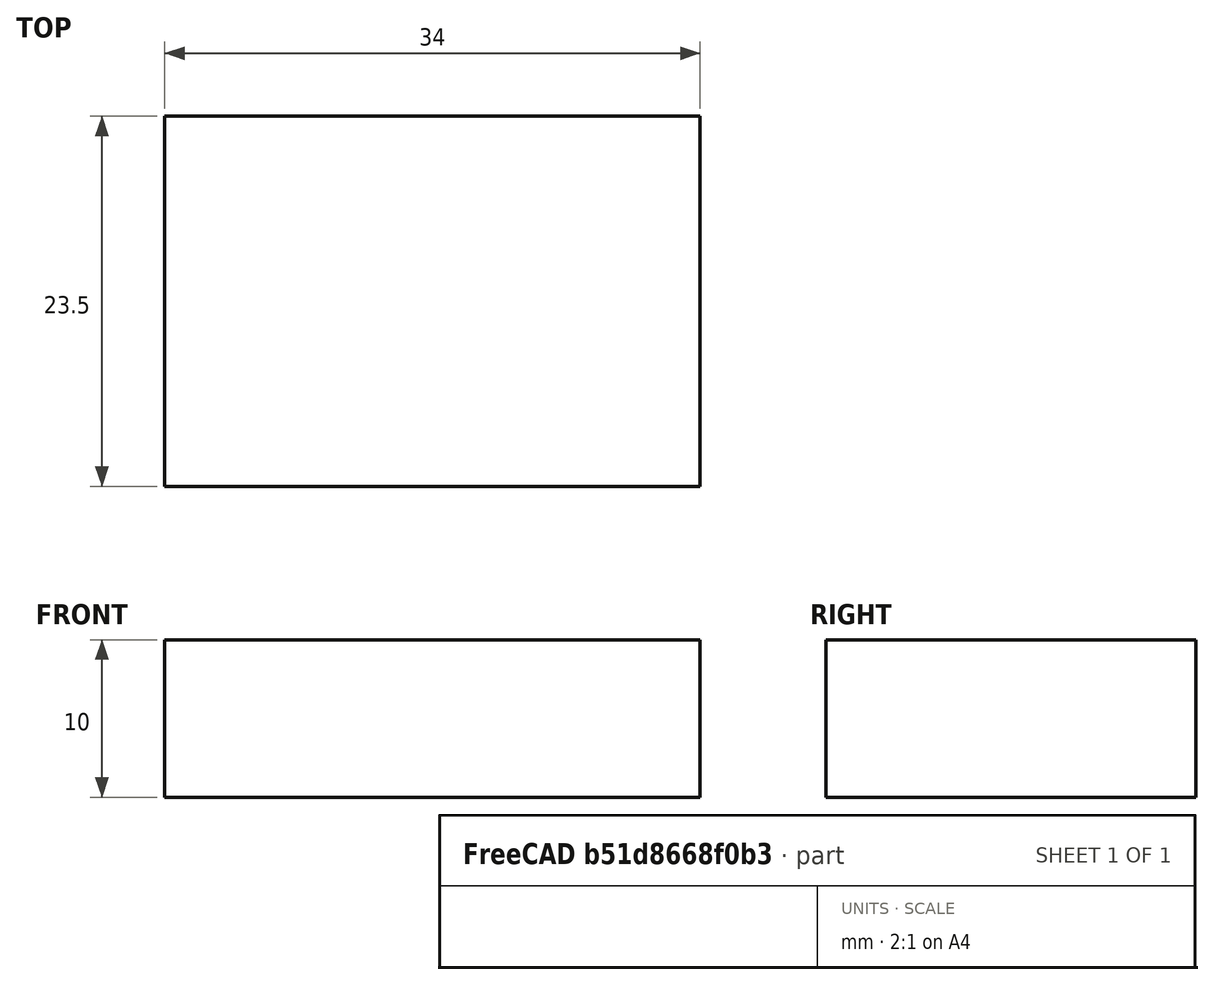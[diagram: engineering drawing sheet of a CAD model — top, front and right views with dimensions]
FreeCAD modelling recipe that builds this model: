
FCSTD DOCUMENT  (FreeCAD 0.18R16131 (Git))
Label: Limit Switch Bed - Top Job
License: All rights reserved
LicenseURL: http://es.wikipedia.org/wiki/Todos_los_derechos_reservados
objects: Path::FeaturePython×16, Part::FeaturePython×2, App::FeaturePython×1, Part::Feature×1, App::DocumentObjectGroup×1, Path::FeatureCompoundPython×1, Mesh::FeaturePython×1
note: 8 computed .brp shape members not serialized (recipe doc carries the construction recipe); baked Part::Feature solids carry a one-line shape summary decoded from their .brp

FEATURE [App::FeaturePython] SetupSheet  # Path/CAM operation (typed FeaturePython)
  ClearanceHeightExpression = OpStockZMax+SetupSheet.ClearanceHeightOffset
  ClearanceHeightOffset = 5
  FinalDepthExpression = OpFinalDepth
  HorizRapid = 0
  SafeHeightExpression = OpStockZMax+SetupSheet.SafeHeightOffset
  SafeHeightOffset = 3
  StartDepthExpression = OpStartDepth
  StepDownExpression = OpToolDiameter
  VertRapid = 0
FEATURE [Path::FeaturePython] T3__SingleFlute2mm  label="T3: SingleFlute2mm"  # Path/CAM operation (typed FeaturePython)
  HorizFeed = 0
  HorizRapid = 0
  SpindleDir = 0
  SpindleSpeed = 0
  ToolNumber = 3
  VertFeed = 0
  VertRapid = 0
  expr: HorizRapid = SetupSheet.HorizRapid
  expr: VertRapid = SetupSheet.VertRapid
FEATURE [Path::FeaturePython] T4__CornTeeth1mm  label="T4: SingleFlute1mm"  # Path/CAM operation (typed FeaturePython)
  HorizFeed = 25
  HorizRapid = 0
  SpindleDir = 0
  SpindleSpeed = 8000
  ToolNumber = 4
  VertFeed = 5
  VertRapid = 0
  expr: HorizRapid = SetupSheet.HorizRapid
  expr: VertRapid = SetupSheet.VertRapid
FEATURE [Path::FeaturePython] T5__Drill1mml  label="T5: Drill1mml"  # Path/CAM operation (typed FeaturePython)
  HorizFeed = 0
  HorizRapid = 0
  SpindleDir = 0
  SpindleSpeed = 0
  ToolNumber = 5
  VertFeed = 0
  VertRapid = 0
  expr: HorizRapid = SetupSheet.HorizRapid
  expr: VertRapid = SetupSheet.VertRapid
FEATURE [Path::FeaturePython] T6__Drill2mm  label="T6: Drill2mm"  # Path/CAM operation (typed FeaturePython)
  HorizFeed = 0
  HorizRapid = 0
  SpindleDir = 0
  SpindleSpeed = 0
  ToolNumber = 6
  VertFeed = 0
  VertRapid = 0
  expr: HorizRapid = SetupSheet.HorizRapid
  expr: VertRapid = SetupSheet.VertRapid
FEATURE [Path::FeaturePython] Contour  label="Interior Contour"  # Path/CAM operation (typed FeaturePython)
  Active = true
  AreaParams:
    Tolerance = 1e-07
    FitArcs = True
    Simplify = False
    CleanDistance = 0.0
    Accuracy = 0.01
    Unit = 1.0
    MinArcPoints = 4
    MaxArcPoints = 100
    ClipperScale = 10000000.0
    Fill = 0
    Coplanar = 2
    Reorient = True
    Outline = False
    Explode = False
    OpenMode = 0
    Deflection = 0.01
    SubjectFill = 0
    ClipFill = 0
    Offset = 0.5
    ExtraPass = 0
    Stepover = 0.0
    LastStepover = 0.0
    JoinType = 0
    EndType = 0
    MiterLimit = 2.0
    RoundPrecision = 0.0
    PocketMode = 0
    ToolRadius = 1.0
    PocketExtraOffset = 0.0
    PocketStepover = 0.0
    PocketLastStepover = 0.0
    FromCenter = False
    Angle = 45.0
    AngleShift = 0.0
    Shift = 0.0
    Thicken = False
    SectionCount = -1
    Stepdown = 1.0
    SectionOffset = 0.0
    SectionTolerance = 1e-06
    SectionMode = 2
    Project = False
  ClearanceHeight = 15
  Direction = 0
  FinalDepth = 3
  JoinType = 0
  MiterLimit = 0.1
  OffsetExtra = 0
  OpFinalDepth = 0
  OpStartDepth = 10
  OpStockZMax = 10
  OpStockZMin = 0
  OpToolDiameter = 1
  PathParams = {'orientation': 1, 'feedrate': 25.0, 'feedrate_v': 5.0, 'verbose': True, 'resume_height': 13.0, 'retraction': 15.0, 'return_end': True, 'preamble': False}
  SafeHeight = 13
  Side = 0
  StartDepth = 10
  StartPoint = (0,0,0)
  StepDown = 1
  ToolController = -> T4__CornTeeth1mm
  UseComp = true
  UseStartPoint = false
  expr: ClearanceHeight = OpStockZMax + SetupSheet.ClearanceHeightOffset
  expr: SafeHeight = OpStockZMax + SetupSheet.SafeHeightOffset
  expr: StepDown = OpToolDiameter
  expr: FinalDepth = 3
  expr: StartDepth = OpStartDepth
FEATURE [Path::FeaturePython] Contour001  label="Exterior Contour"  # Path/CAM operation (typed FeaturePython)
  Active = true
  AreaParams:
    Tolerance = 1e-07
    FitArcs = True
    Simplify = False
    CleanDistance = 0.0
    Accuracy = 0.01
    Unit = 1.0
    MinArcPoints = 4
    MaxArcPoints = 100
    ClipperScale = 10000000.0
    Fill = 0
    Coplanar = 2
    Reorient = True
    Outline = False
    Explode = False
    OpenMode = 0
    Deflection = 0.01
    SubjectFill = 0
    ClipFill = 0
    Offset = 0.7
    ExtraPass = 0
    Stepover = 0.0
    LastStepover = 0.0
    JoinType = 0
    EndType = 0
    MiterLimit = 2.0
    RoundPrecision = 0.0
    PocketMode = 0
    ToolRadius = 1.0
    PocketExtraOffset = 0.0
    PocketStepover = 0.0
    PocketLastStepover = 0.0
    FromCenter = False
    Angle = 45.0
    AngleShift = 0.0
    Shift = 0.0
    Thicken = False
    SectionCount = -1
    Stepdown = 1.0
    SectionOffset = 0.0
    SectionTolerance = 1e-06
    SectionMode = 2
    Project = False
  ClearanceHeight = 15
  Direction = 0
  FinalDepth = 3
  JoinType = 0
  MiterLimit = 0.1
  OffsetExtra = 0.2
  OpFinalDepth = 0
  OpStartDepth = 10
  OpStockZMax = 10
  OpStockZMin = 0
  OpToolDiameter = 1
  PathParams = {'orientation': 1, 'feedrate': 25.0, 'feedrate_v': 5.0, 'verbose': True, 'resume_height': 13.0, 'retraction': 15.0, 'return_end': True, 'preamble': False}
  SafeHeight = 13
  Side = 0
  StartDepth = 10
  StartPoint = (0,0,0)
  StepDown = 3
  ToolController = -> T4__CornTeeth1mm
  UseComp = true
  UseStartPoint = false
  expr: ClearanceHeight = OpStockZMax + SetupSheet.ClearanceHeightOffset
  expr: SafeHeight = OpStockZMax + SetupSheet.SafeHeightOffset
  expr: StepDown = 3
  expr: FinalDepth = 3
  expr: StartDepth = OpStartDepth
FEATURE [Path::FeaturePython] Contour002  # Path/CAM operation (typed FeaturePython)
  Active = true
  AreaParams:
    Tolerance = 1e-07
    FitArcs = True
    Simplify = False
    CleanDistance = 0.0
    Accuracy = 0.01
    Unit = 1.0
    MinArcPoints = 4
    MaxArcPoints = 100
    ClipperScale = 10000000.0
    Fill = 0
    Coplanar = 2
    Reorient = True
    Outline = False
    Explode = False
    OpenMode = 0
    Deflection = 0.01
    SubjectFill = 0
    ClipFill = 0
    Offset = 0.6
    ExtraPass = 0
    Stepover = 0.0
    LastStepover = 0.0
    JoinType = 0
    EndType = 0
    MiterLimit = 2.0
    RoundPrecision = 0.0
    PocketMode = 0
    ToolRadius = 1.0
    PocketExtraOffset = 0.0
    PocketStepover = 0.0
    PocketLastStepover = 0.0
    FromCenter = False
    Angle = 45.0
    AngleShift = 0.0
    Shift = 0.0
    Thicken = False
    SectionCount = -1
    Stepdown = 1.0
    SectionOffset = 0.0
    SectionTolerance = 1e-06
    SectionMode = 2
    Project = False
  ClearanceHeight = 15
  Direction = 0
  FinalDepth = 0
  JoinType = 0
  MiterLimit = 0.1
  OffsetExtra = 0.1
  OpFinalDepth = 0
  OpStartDepth = 10
  OpStockZMax = 10
  OpStockZMin = 0
  OpToolDiameter = 1
  PathParams = {'orientation': 1, 'feedrate': 25.0, 'feedrate_v': 5.0, 'verbose': True, 'resume_height': 13.0, 'retraction': 15.0, 'return_end': True, 'preamble': False}
  SafeHeight = 13
  Side = 0
  StartDepth = 3
  StartPoint = (0,0,0)
  StepDown = 1
  ToolController = -> T4__CornTeeth1mm
  UseComp = true
  UseStartPoint = false
  expr: ClearanceHeight = OpStockZMax + SetupSheet.ClearanceHeightOffset
  expr: SafeHeight = OpStockZMax + SetupSheet.SafeHeightOffset
  expr: StepDown = OpToolDiameter
  expr: FinalDepth = OpFinalDepth
  expr: StartDepth = 3
FEATURE [Path::FeaturePython] TagDressup  label="Bottom Contourn"  # Path/CAM operation (typed FeaturePython)
  Angle = 60
  Base = -> Contour002
  Height = 0.5
  Positions = (5) [(24,-0.6,0),(8,-0.6,0),(-0.6,10.75,0),(8.5,22.1,0),(32.6,10,0)]
  Radius = 0
  SegmentationFactor = 50
  Width = 1.5
FEATURE [Part::Feature] Part__Feature  label="LimitSwitchBed"
  shape: bbox 32 x 21.5 x 10 mm, 57 faces (baked)
FEATURE [Part::FeaturePython] Clone  label="Model-Body"  # Draft clone (typed FeaturePython)
  AttacherType = Attacher::AttachEngine3D
  Fuse = false
  Objects = -> [Part__Feature]
  PathResource = Model
  Scale = (1,1,1)
FEATURE [App::DocumentObjectGroup] Model
  Group = -> [Clone]
FEATURE [Part::FeaturePython] Stock  # WARN: FeaturePython — macro-defined, semantics opaque (R4)
  Base = -> Model
  ExtXneg = 1
  ExtXpos = 1
  ExtYneg = 1
  ExtYpos = 1
  ExtZneg = 0
  ExtZpos = 0
  StockType = FromBase
FEATURE [Path::FeaturePython] Pocket_Shape001  # Path/CAM operation (typed FeaturePython)
  Active = true
  AreaParams:
    Tolerance = 1e-07
    FitArcs = True
    Simplify = False
    CleanDistance = 0.0
    Accuracy = 0.01
    Unit = 1.0
    MinArcPoints = 4
    MaxArcPoints = 100
    ClipperScale = 10000000.0
    Fill = 0
    Coplanar = 0
    Reorient = True
    Outline = False
    Explode = False
    OpenMode = 0
    Deflection = 0.01
    SubjectFill = 0
    ClipFill = 0
    Offset = 0.0
    ExtraPass = 0
    Stepover = 0.0
    LastStepover = 0.0
    JoinType = 0
    EndType = 0
    MiterLimit = 2.0
    RoundPrecision = 0.0
    PocketMode = 3
    ToolRadius = 0.5
    PocketExtraOffset = 0.0
    PocketStepover = 1.0
    PocketLastStepover = 0.0
    FromCenter = True
    Angle = 45.0
    AngleShift = 0.0
    Shift = 0.0
    Thicken = False
    SectionCount = -1
    Stepdown = 1.0
    SectionOffset = 0.0
    SectionTolerance = 1e-06
    SectionMode = 2
    Project = False
  Base = -> [Clone]
  ClearanceHeight = 15
  CutMode = 0
  ExtraOffset = 0
  FinalDepth = 6
  FinishDepth = 0
  KeepToolDown = false
  MinTravel = false
  OffsetPattern = 2
  OpFinalDepth = 6
  OpStartDepth = 10
  OpStockZMax = 10
  OpStockZMin = 0
  OpToolDiameter = 1
  PathParams = {'orientation': 1, 'feedrate': 25.0, 'feedrate_v': 5.0, 'verbose': True, 'resume_height': 13.0, 'retraction': 15.0, 'return_end': True, 'preamble': False}
  SafeHeight = 13
  StartAt = 0
  StartDepth = 10
  StartPoint = (0,0,0)
  StepDown = 0.5
  StepOver = 100
  ToolController = -> T4__CornTeeth1mm
  UseOutline = false
  UseStartPoint = false
  ZigZagAngle = 45
  expr: ClearanceHeight = OpStockZMax + SetupSheet.ClearanceHeightOffset
  expr: SafeHeight = OpStockZMax + SetupSheet.SafeHeightOffset
  expr: StepDown = OpToolDiameter / 2
  expr: FinalDepth = OpFinalDepth
  expr: StartDepth = OpStartDepth
FEATURE [Path::FeaturePython] Pocket_Shape  # Path/CAM operation (typed FeaturePython)
  Active = true
  AreaParams:
    Tolerance = 1e-07
    FitArcs = True
    Simplify = False
    CleanDistance = 0.0
    Accuracy = 0.01
    Unit = 1.0
    MinArcPoints = 4
    MaxArcPoints = 100
    ClipperScale = 10000000.0
    Fill = 0
    Coplanar = 0
    Reorient = True
    Outline = False
    Explode = False
    OpenMode = 0
    Deflection = 0.01
    SubjectFill = 0
    ClipFill = 0
    Offset = 0.0
    ExtraPass = 0
    Stepover = 0.0
    LastStepover = 0.0
    JoinType = 0
    EndType = 0
    MiterLimit = 2.0
    RoundPrecision = 0.0
    PocketMode = 2
    ToolRadius = 0.5
    PocketExtraOffset = 0.0
    PocketStepover = 0.5
    PocketLastStepover = 0.0
    FromCenter = True
    Angle = 45.0
    AngleShift = 0.0
    Shift = 0.0
    Thicken = False
    SectionCount = -1
    Stepdown = 1.0
    SectionOffset = 0.0
    SectionTolerance = 1e-06
    SectionMode = 2
    Project = False
  Base = -> [Clone]
  ClearanceHeight = 15
  CutMode = 0
  ExtraOffset = 0
  FinalDepth = 4
  FinishDepth = 0
  KeepToolDown = false
  MinTravel = false
  OffsetPattern = 1
  OpFinalDepth = 4
  OpStartDepth = 10
  OpStockZMax = 10
  OpStockZMin = 0
  OpToolDiameter = 1
  PathParams = {'orientation': 1, 'feedrate': 25.0, 'feedrate_v': 5.0, 'verbose': True, 'resume_height': 13.0, 'retraction': 15.0, 'return_end': True, 'preamble': False}
  SafeHeight = 13
  StartAt = 0
  StartDepth = 10
  StartPoint = (0,0,0)
  StepDown = 1
  StepOver = 50
  ToolController = -> T4__CornTeeth1mm
  UseOutline = false
  UseStartPoint = false
  ZigZagAngle = 45
  expr: ClearanceHeight = OpStockZMax + SetupSheet.ClearanceHeightOffset
  expr: SafeHeight = OpStockZMax + SetupSheet.SafeHeightOffset
  expr: StepDown = OpToolDiameter
  expr: FinalDepth = OpFinalDepth
  expr: StartDepth = OpStartDepth
FEATURE [Path::FeaturePython] DogboneDressup001  label="SwitchBed"  # Path/CAM operation (typed FeaturePython)
  Base = -> Pocket_Shape
  BoneBlacklist = [5,6,7,8,9,10,11,12,13,14,15,16,17,18,19,20,25,26,27,28,29,30,31,32,33,34,39,40,41,42,43,44,45,46,47,48,53,54,55,56,57,58,59,60,61,62,67,68,69,70,71,72,73,74,75,76,81,82,83]
  Custom = 0
  Incision = 0
  Side = 1
  Style = 0
FEATURE [Path::FeaturePython] DogboneDressup  # Path/CAM operation (typed FeaturePython)
  Base = -> Pocket_Shape001
  BoneBlacklist = [1,10,11,20,21,30,31,40,41,50,51,60,61,70,71,80]
  Custom = 0.6
  Incision = 2
  Side = 0
  Style = 2
FEATURE [Path::FeaturePython] DogboneDressup002  # Path/CAM operation (typed FeaturePython)
  Base = -> DogboneDressup
  BoneBlacklist = [2,3,4,5,6,7,8,9,10,11,12,13,14,15,16,17,18,19,20,21,22,23,24,25,26,28,29,30,31,32,33,34,35,36,37,38,39,40,41,42,43,44,45,46,47,48,49,50,51,52,54,55,56,57,58,59,60,61,62,63,64,65,66,67,68,69,70,71,72,+131 more]
  Custom = 0.6
  Incision = 2
  Side = 0
  Style = 4
FEATURE [Path::FeaturePython] Helix  label="WashBed"  # Path/CAM operation (typed FeaturePython)
  Active = true
  Base = -> [Clone]
  ClearanceHeight = 15
  Direction = 0
  FinalDepth = 7.5
  OpFinalDepth = 10
  OpStartDepth = 11
  OpStockZMax = 10
  OpStockZMin = 0
  OpToolDiameter = 1
  SafeHeight = 13
  StartDepth = 10
  StartSide = 0
  StepDown = 1
  StepOver = 90
  ToolController = -> T4__CornTeeth1mm
  expr: ClearanceHeight = OpStockZMax + SetupSheet.ClearanceHeightOffset
  expr: SafeHeight = OpStockZMax + SetupSheet.SafeHeightOffset
  expr: StepDown = OpToolDiameter
  expr: FinalDepth = 7.5
  expr: StartDepth = 10
FEATURE [Path::FeaturePython] Helix001  label="BoltHole"  # Path/CAM operation (typed FeaturePython)
  Active = true
  Base = -> [Clone]
  ClearanceHeight = 15
  Direction = 0
  FinalDepth = 0
  OpFinalDepth = 7
  OpStartDepth = 10
  OpStockZMax = 10
  OpStockZMin = 0
  OpToolDiameter = 1
  SafeHeight = 13
  StartDepth = 7
  StartSide = 0
  StepDown = 1
  StepOver = 100
  ToolController = -> T4__CornTeeth1mm
  expr: ClearanceHeight = OpStockZMax + SetupSheet.ClearanceHeightOffset
  expr: SafeHeight = OpStockZMax + SetupSheet.SafeHeightOffset
  expr: StepDown = OpToolDiameter
  expr: FinalDepth = 0
  expr: StartDepth = OpFinalDepth
FEATURE [Path::FeatureCompoundPython] Operations  # Path/CAM operation (typed FeaturePython)
  Group = -> [DogboneDressup002,DogboneDressup001,Contour,Contour001,TagDressup,Helix,Helix001]
  UsePlacements = false
FEATURE [Path::FeaturePython] Job  label="Top-Job"  # Path/CAM operation (typed FeaturePython)
  GeometryTolerance = 0.01
  Model = -> Model
  Operations = -> Operations
  PostProcessor = 5
  PostProcessorOutputFile = <userpath>/github/Limit Switch Bed/LSB-Top.gcode
  SetupSheet = -> SetupSheet
  Stock = -> Stock
  ToolController = -> [T3__SingleFlute2mm,T4__CornTeeth1mm,T5__Drill1mml,T6__Drill2mm]
FEATURE [Mesh::FeaturePython] CutMaterial001  # WARN: FeaturePython — macro-defined, semantics opaque (R4)
